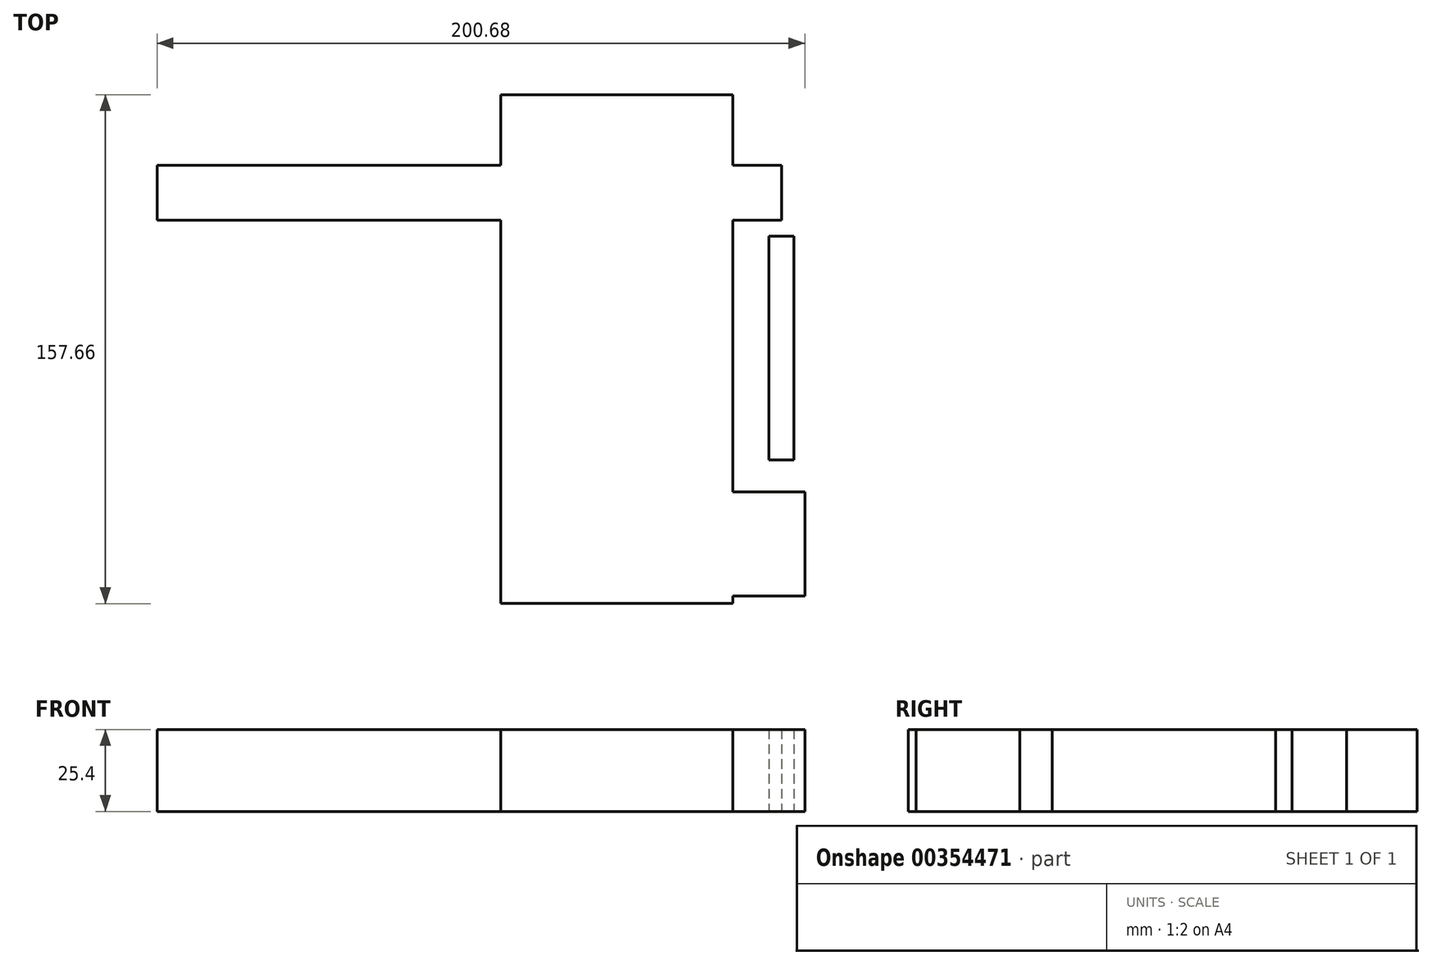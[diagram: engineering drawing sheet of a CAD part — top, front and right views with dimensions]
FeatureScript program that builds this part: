
annotation { "Feature Type Name" : "Feature", "Feature Type Description" : "" }
export const myFeature = defineFeature(function(context is Context, id is Id, definition is map)
    precondition{}
    {
        {
            var Q0;
            Q0=qCreatedBy(makeId("Top.planeOp"),FACE);
            var sketch = newSketch(context, id + "F0", { "sketchPlane" : qUnion([Q0])});
            skLineSegment(sketch, "E0.bottom", {"start": v(-50.65, 55.17) * mm, "end": v(21.25, 55.17) * mm});
            skLineSegment(sketch, "E0.top", {"start": v(-50.65, -102.49) * mm, "end": v(21.25, -102.49) * mm});
            skLineSegment(sketch, "E0.left", {"start": v(-50.65, 55.17) * mm, "end": v(-50.65, -102.49) * mm});
            skLineSegment(sketch, "E0.right", {"start": v(21.25, 55.17) * mm, "end": v(21.25, -102.49) * mm});
            skLineSegment(sketch, "E1.bottom", {"start": v(21.25, -67.92) * mm, "end": v(43.62, -67.92) * mm});
            skLineSegment(sketch, "E1.top", {"start": v(21.25, -100.12) * mm, "end": v(43.62, -100.12) * mm});
            skLineSegment(sketch, "E1.left", {"start": v(21.25, -67.92) * mm, "end": v(21.25, -100.12) * mm});
            skLineSegment(sketch, "E1.right", {"start": v(43.62, -67.92) * mm, "end": v(43.62, -100.12) * mm});
            skPoint(sketch, "E2.firstSnap0", {"position": v(32.44, -67.92) * mm});
            skLineSegment(sketch, "E2.bottom", {"start": v(32.44, -57.95) * mm, "end": v(40.26, -57.95) * mm});
            skLineSegment(sketch, "E2.top", {"start": v(32.44, 11.37) * mm, "end": v(40.26, 11.37) * mm});
            skLineSegment(sketch, "E2.left", {"start": v(32.44, -57.95) * mm, "end": v(32.44, 11.37) * mm});
            skLineSegment(sketch, "E2.right", {"start": v(40.26, -57.95) * mm, "end": v(40.26, 11.37) * mm});
            skLineSegment(sketch, "E3.bottom", {"start": v(36.38, 16.38) * mm, "end": v(-157.06, 16.38) * mm});
            skLineSegment(sketch, "E3.top", {"start": v(36.38, 33.3) * mm, "end": v(-157.06, 33.3) * mm});
            skLineSegment(sketch, "E3.left", {"start": v(36.38, 16.38) * mm, "end": v(36.38, 33.3) * mm});
            skLineSegment(sketch, "E3.right", {"start": v(-157.06, 16.38) * mm, "end": v(-157.06, 33.3) * mm});
            skSolve(sketch);
        }
        {
            var Q0;
            Q0=makeQuery(id+"F0.imprint","IMPRINT",FACE,{"disambiguationData":[TD([[makeQuery(id+"F0.imprint","IMPRINT",EDGE,{"derivedFrom":sQuery(id+"F0.wireOp",EDGE,"E2.bottom")}),1.0]])]});
            var Q1;
            {var subQ0=sQuery(id+"F0.wireOp",EDGE,"E0.bottom");Q1=makeQuery(id+"F0.imprint","IMPRINT",FACE,{"disambiguationData":[TD([[makeQuery(id+"F0.imprint","IMPRINT",EDGE,{"derivedFrom":subQ0}),-1.0]])]});}
            var Q2;
            {var subQ5=sQuery(id+"F0.wireOp",EDGE,"E3.right");Q2=makeQuery(id+"F0.imprint","IMPRINT",FACE,{"disambiguationData":[TD([[makeQuery(id+"F0.imprint","IMPRINT",EDGE,{"derivedFrom":subQ5}),-1.0]])]});}
            var Q3;
            {var subQ5=sQuery(id+"F0.wireOp",EDGE,"E3.left");Q3=makeQuery(id+"F0.imprint","IMPRINT",FACE,{"disambiguationData":[TD([[makeQuery(id+"F0.imprint","IMPRINT",EDGE,{"derivedFrom":subQ5}),1.0]])]});}
            var Q4;
            Q4=makeQuery(id+"F0.imprint","IMPRINT",FACE,{"disambiguationData":[TD([[makeQuery(id+"F0.imprint","IMPRINT",EDGE,{"derivedFrom":sQuery(id+"F0.wireOp",EDGE,"E1.bottom")}),-1.0]])]});
            var Q5;
            {var subQ0=sQuery(id+"F0.wireOp",EDGE,"E3.top");var subQ1=sQuery(id+"F0.wireOp",EDGE,"E0.left");var subQ2=makeQuery(id+"F0.imprint","INTERSECT",VERTEX,{"derivedFrom":[subQ1,subQ0]});Q5=makeQuery(id+"F0.imprint","IMPRINT",FACE,{"disambiguationData":[TD([[makeQuery(id+"F0.imprint","IMPRINT",EDGE,{"disambiguationData":[TD([[subQ2,-1.0]])],"derivedFrom":subQ1}),1.0]])]});}
            var Q6;
            {var subQ1=sQuery(id+"F0.wireOp",EDGE,"E0.top");Q6=makeQuery(id+"F0.imprint","IMPRINT",FACE,{"disambiguationData":[TD([[makeQuery(id+"F0.imprint","IMPRINT",EDGE,{"derivedFrom":subQ1}),1.0]])]});}
            extrude(context, id + "F1", {"entities" : qUnion([Q0, Q1, Q2, Q3, Q4, Q5, Q6]), "endBound" : BoundingType.SYMMETRIC, "depth" : 25.4 * mm});
        }
    });
